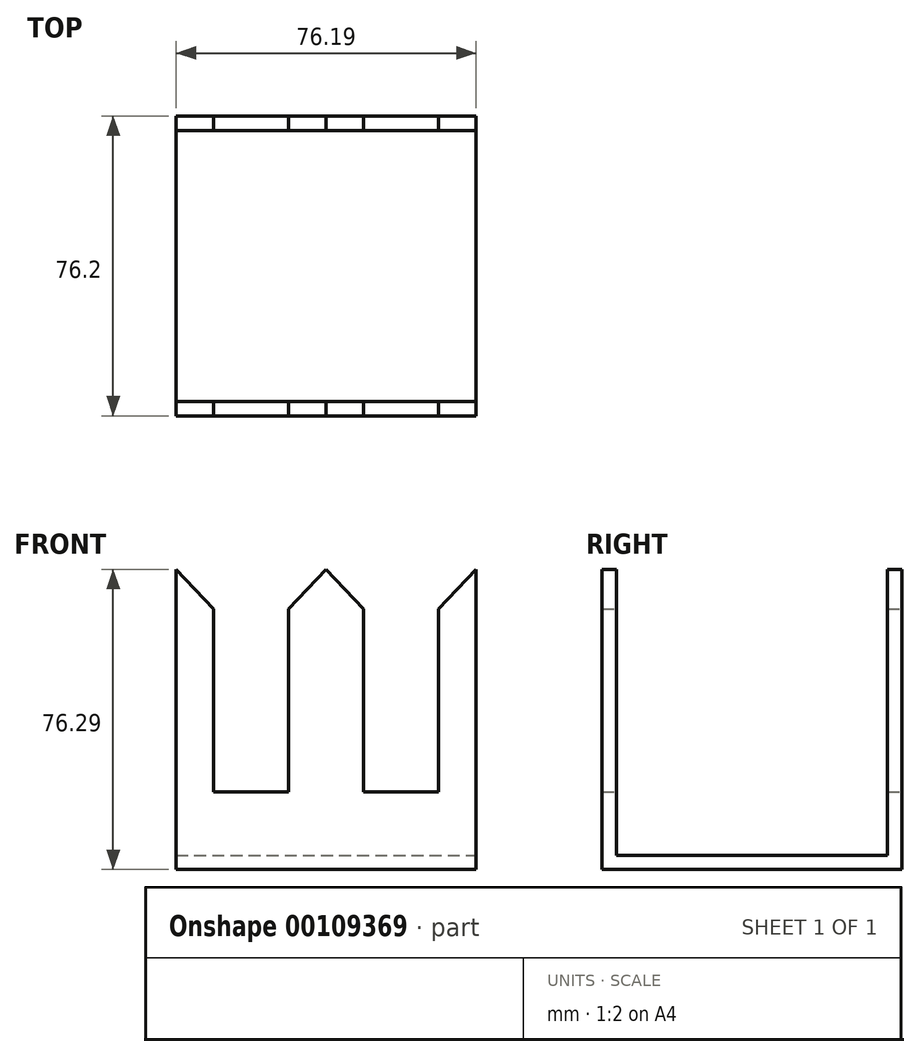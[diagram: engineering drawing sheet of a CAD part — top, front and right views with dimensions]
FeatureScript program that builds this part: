
annotation { "Feature Type Name" : "Feature", "Feature Type Description" : "" }
export const myFeature = defineFeature(function(context is Context, id is Id, definition is map)
    precondition{}
    {
        {
            var Q0;
            Q0=qCreatedBy(makeId("Front.planeOp"),FACE);
            var sketch = newSketch(context, id + "F0", { "sketchPlane" : qUnion([Q0])});
            skLineSegment(sketch, "E0.top", {"start": v(0, 0) * mm, "end": v(76.2, 0) * mm});
            skLineSegment(sketch, "E0.left", {"start": v(0, 76.29) * mm, "end": v(0, 0) * mm});
            skLineSegment(sketch, "E0.right", {"start": v(76.2, 76.29) * mm, "end": v(76.2, 0) * mm});
            skLineSegment(sketch, "E1.bottom", {"start": v(38.1, 76.29) * mm, "end": v(38.1, 76.29) * mm});
            skLineSegment(sketch, "E1.top", {"start": v(38.1, 0) * mm, "end": v(38.1, 0) * mm});
            skLineSegment(sketch, "E2", {"start": v(0, 76.29) * mm, "end": v(9.52, 66.2) * mm});
            skLineSegment(sketch, "E3", {"start": v(28.57, 66.2) * mm, "end": v(38.1, 76.29) * mm});
            skLineSegment(sketch, "E4", {"start": v(9.52, 19.68) * mm, "end": v(28.57, 19.68) * mm});
            skLineSegment(sketch, "E5", {"start": v(9.52, 66.2) * mm, "end": v(9.52, 19.68) * mm});
            skLineSegment(sketch, "E6", {"start": v(28.57, 66.2) * mm, "end": v(28.57, 19.68) * mm});
            skPoint(sketch, "E7.end.orphan", {"position": v(19.05, 76.29) * mm});
            skPoint(sketch, "E7.start.orphan", {"position": v(19.05, 56.11) * mm});
            skPoint(sketch, "E8.orphan", {"position": v(38.1, 19.68) * mm});
            skPoint(sketch, "E9.orphan", {"position": v(38.1, 56.11) * mm});
            skPoint(sketch, "E10.orphan", {"position": v(0, 56.11) * mm});
            skLineSegment(sketch, "E11.MirrorCS", {"start": v(47.62, 66.2) * mm, "end": v(38.1, 76.29) * mm});
            skLineSegment(sketch, "E12.MirrorCS", {"start": v(47.62, 66.2) * mm, "end": v(47.62, 19.68) * mm});
            skLineSegment(sketch, "E13.MirrorCS", {"start": v(66.67, 19.68) * mm, "end": v(47.62, 19.68) * mm});
            skLineSegment(sketch, "E14.MirrorCS", {"start": v(66.67, 66.2) * mm, "end": v(66.67, 19.68) * mm});
            skLineSegment(sketch, "E15.MirrorCS", {"start": v(76.2, 76.29) * mm, "end": v(66.67, 66.2) * mm});
            skSolve(sketch);
        }
        {
            var Q0;
            Q0 = qSketchRegion(id + "F0", true);
            extrude(context, id + "F1", {"entities" : qUnion([Q0]), "depth" : 76.2 * mm});
        }
        {
            var Q0;
            Q0=makeQuery(id+"F1.opExtrude","SWEPT_FACE",FACE,{"disambiguationData":[OSD([sQuery(id+"F0.wireOp",EDGE,"E0.right")])]});
            var sketch = newSketch(context, id + "F2", { "sketchPlane" : qUnion([Q0])});
            skLineSegment(sketch, "E16.bottom", {"start": v(-72.59, 81.18) * mm, "end": v(-3.7, 81.18) * mm});
            skLineSegment(sketch, "E16.top", {"start": v(-72.59, 3.65) * mm, "end": v(-3.7, 3.65) * mm});
            skLineSegment(sketch, "E16.left", {"start": v(-72.59, 81.18) * mm, "end": v(-72.59, 3.65) * mm});
            skLineSegment(sketch, "E16.right", {"start": v(-3.7, 81.18) * mm, "end": v(-3.7, 3.65) * mm});
            skSolve(sketch);
        }
        {
            var Q0;
            {var subQ0=sQuery(id+"F2.wireOp",EDGE,"E16.bottom");Q0=makeQuery(id+"F2.imprint","IMPRINT",FACE,{"disambiguationData":[TD([[makeQuery(id+"F2.imprint","IMPRINT",EDGE,{"derivedFrom":subQ0}),-1.0]])]});}
            var Q1;
            {var subQ0=sQuery(id+"F2.wireOp",EDGE,"E16.top");Q1=makeQuery(id+"F2.imprint","IMPRINT",FACE,{"disambiguationData":[TD([[makeQuery(id+"F2.imprint","IMPRINT",EDGE,{"derivedFrom":subQ0}),1.0]])]});}
            extrude(context, id + "F3", {"entities" : qUnion([Q0, Q1]), "operationType" : NewBodyOperationType.REMOVE, "oppositeDirection" : true, "depth" : 88.9 * mm});
        }
    });
